# Revit family: Haworth_ActiveComponents_RectangleConvergentHalfConferenceEnd_BUILD2
name_source: partatom
category: Furniture Systems
revit_build: Autodesk Revit Architecture 2015 (Build: 20141119_1515(x64)
units: mm (PartAtom-declared; Revit-internal decimal feet)

## types (2) — shared parameters
Actual Depth = 33"
Actual Height = 29 3/16"
Angled Leg Offset = 5 3/8"
Assembly Code = E2020200
Depth = 33"
Description = Haworth - Active Components - Rectangular Convergent Half Conference End
Leg F/B Offset = 8 1/8"
Manufacturer = Haworth
Max. Depth = 33"
Max. Width = 72"
Min. Depth = 33"
Min. Width = 60"
Model = WAYJ
Radius = 3"
Revision Number = 1
Size = Verify Final Dim. w/ Haworth
Thickness = 1 3/16"
URL = www.haworth.com
URL - Product = https://www.haworth.com
Warranty = https://www.haworth.com
With Leg = Yes

## per-type parameters (varying)
| type | Actual Width | Width |
| 33d 72w | 72" | 72" |
| 33d 60w | 60" | 60" |

## geometry (parser evidence)
native form markers: Blend x41, Sweep x7
no freeform markers — native parametric forms only
